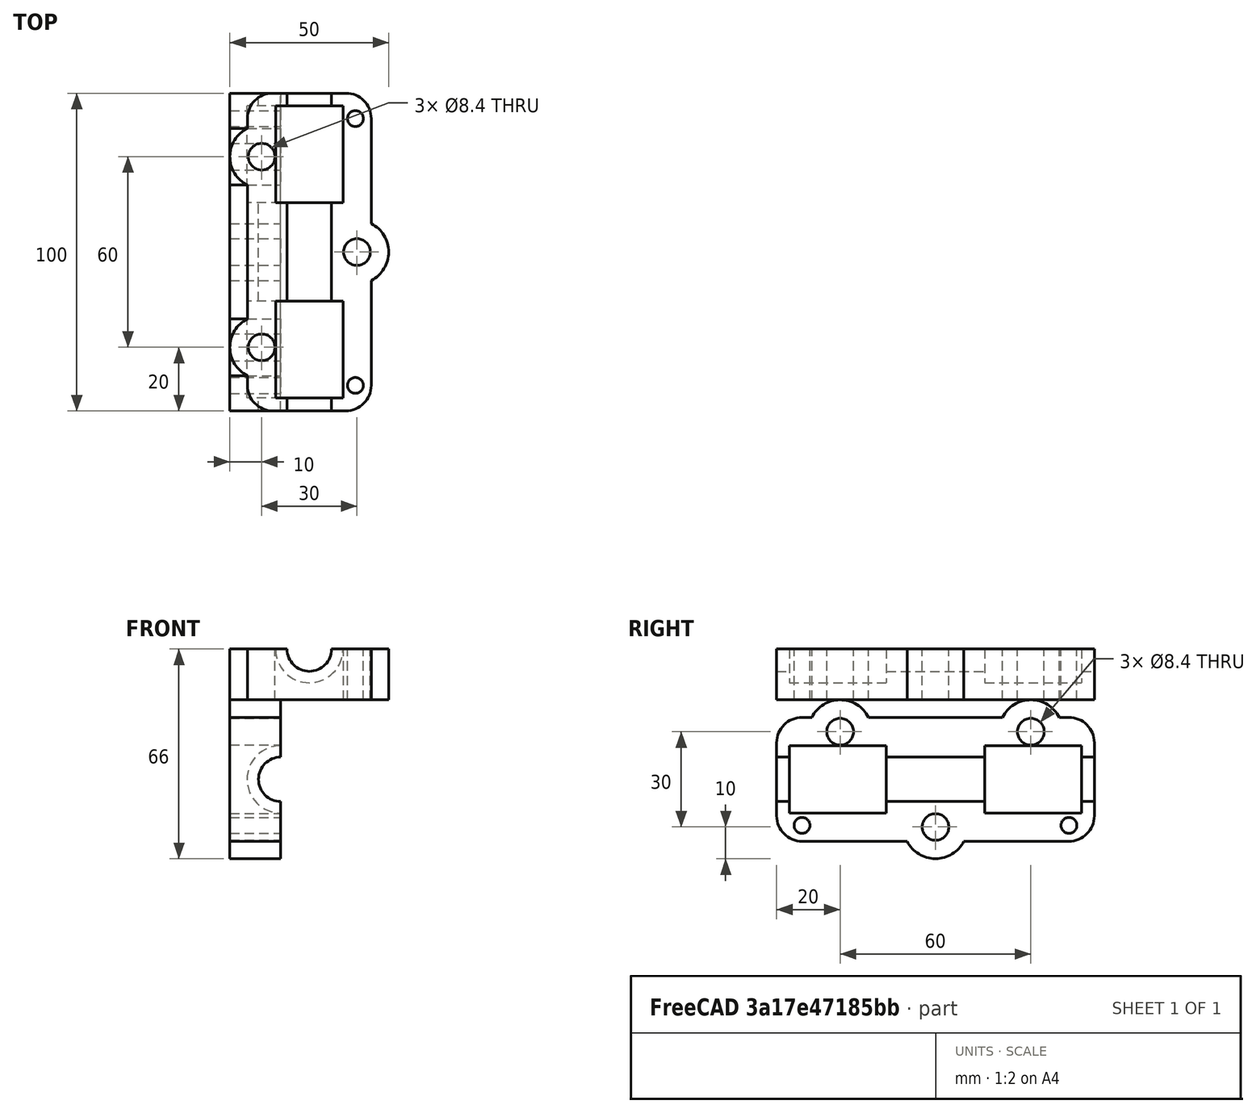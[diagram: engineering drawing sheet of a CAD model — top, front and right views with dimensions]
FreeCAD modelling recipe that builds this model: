
FCSTD DOCUMENT  (FreeCAD 0.15R4666 (Git))
Label: y_carriage_B
License: All rights reserved
LicenseURL: http://en.wikipedia.org/wiki/All_rights_reserved
objects: Part::Cylinder×11, Part::MultiFuse×4, Part::Cut×4, Part::Feature×2, Mesh::Feature×1, Part::Box×1, Part::Fillet×1
note: 23 computed .brp shape members not serialized (recipe doc carries the construction recipe); baked Part::Feature solids carry a one-line shape summary decoded from their .brp

FEATURE [Mesh::Feature] Ycariage_12mm
FEATURE [Part::Feature] Ycariage_12mm001001  label="Ycariage_12mm002"
  shape: bbox 50 x 100 x 16 mm, 1602 faces, 0 solids (baked)
FEATURE [Part::Box] Box  label="Cubo"
  Height = 16
  Length = 39
  Placement = pos=(5.5,0,0) rot=(0,0,1;0rad)
  Width = 100
FEATURE [Part::Cylinder] Cylinder  label="Cilindro"
  Angle = 360
  Height = 16
  Placement = pos=(10,20,0) rot=(0,0,1;0rad)
  Radius = 10
FEATURE [Part::Cylinder] Cylinder001  label="Cilindro001"
  Angle = 360
  Height = 16
  Placement = pos=(10,80,0) rot=(0,0,1;0rad)
  Radius = 10
FEATURE [Part::Cylinder] Cylinder002  label="Cilindro002"
  Angle = 360
  Height = 16
  Placement = pos=(40,50,0) rot=(0,0,1;0rad)
  Radius = 10
FEATURE [Part::MultiFuse] Fusion  label="body_1"
  Shapes = -> [Cylinder,Box,Cylinder001,Cylinder002]
FEATURE [Part::Fillet] Fillet
  Base = -> Fusion
  Edges = 4 edges r=8: [Edge2,Edge4,Edge33,Edge35]
FEATURE [Part::Cylinder] Cylinder003  label="threaded_rod_hole_1"
  Angle = 360
  Height = 18
  Placement = pos=(10,20,-1) rot=(0,0,1;0rad)
  Radius = 4.2
FEATURE [Part::Cylinder] Cylinder004  label="threaded_rod_hole_002"
  Angle = 360
  Height = 18
  Placement = pos=(40,50,-1) rot=(0,0,1;0rad)
  Radius = 4.2
FEATURE [Part::Cylinder] Cylinder005  label="threaded_rod_hole_003"
  Angle = 360
  Height = 18
  Placement = pos=(10,80,-1) rot=(0,0,1;0rad)
  Radius = 4.2
FEATURE [Part::MultiFuse] Fusion001  label="threaded_rod_holes"
  Shapes = -> [Cylinder003,Cylinder004,Cylinder005]
FEATURE [Part::Cut] Cut  label="body_tr_holes"
  Base = -> Fillet
  Tool = -> Fusion001
FEATURE [Part::Cylinder] Cylinder006  label="screw_hole_1"
  Angle = 360
  Height = 18
  Placement = pos=(39.5,8,-1) rot=(0,0,1;0rad)
  Radius = 2.5
FEATURE [Part::Cylinder] Cylinder007  label="screw_hole_002"
  Angle = 360
  Height = 18
  Placement = pos=(39.5,92,-1) rot=(0,0,1;0rad)
  Radius = 2.5
FEATURE [Part::MultiFuse] Fusion002  label="screw_holes"
  Shapes = -> [Cylinder006,Cylinder007]
FEATURE [Part::Cut] Cut001  label="body_trsc_holes"
  Base = -> Cut
  Tool = -> Fusion002
FEATURE [Part::Cylinder] Cylinder008  label="threaded_rod_hole"
  Angle = 360
  Height = 102
  Placement = pos=(25,-1,16) rot=(-1,0,0;1.5708rad)
  Radius = 7
FEATURE [Part::Cut] Cut002  label="body_thscth_holes"
  Base = -> Cut001
  Tool = -> Cylinder008
FEATURE [Part::Cylinder] Cylinder009  label="bearing_hole_1"
  Angle = 360
  Height = 30.5
  Placement = pos=(25,4,16) rot=(-1,0,0;1.5708rad)
  Radius = 10.6
FEATURE [Part::Cylinder] Cylinder010  label="bearing_hole_002"
  Angle = 360
  Height = 30.5
  Placement = pos=(25,65.5,16) rot=(-1,0,0;1.5708rad)
  Radius = 10.6
FEATURE [Part::MultiFuse] Fusion003  label="bearing_holes"
  Shapes = -> [Cylinder009,Cylinder010]
FEATURE [Part::Cut] Cut003  label="y_carriage_B"
  Base = -> Cut002
  Tool = -> Fusion003
FEATURE [Part::Feature] Cut003_solid  label="y_carriage_B (Solid)"
  Placement = pos=(0,0,0) rot=(0,1,0;1.5708rad)
  shape: bbox 16 x 100 x 50 mm, 31 faces (baked)
